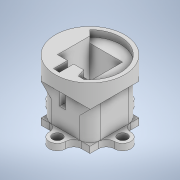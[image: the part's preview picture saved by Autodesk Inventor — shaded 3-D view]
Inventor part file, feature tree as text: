
AUTODESK INVENTOR PART (.ipt)
format: ipt  version: 2022 (Build 260153000, 153)  size: 370,688 bytes
history: native  units: in
note: dims shown in document units (in); Inventor stores cm internally (conversion verified against a paired STEP export)
features: projected_geometry x8, extrude x7, sketch x7, chamfer x2, fillet x2
ambient origin geometry x8: Origin, YZ Plane, XZ Plane, XY Plane, X Axis, Y Axis, Z Axis, Center Point
bodies: Solid1 (feature_tree)
feature tree (26):
  extrude  "Extrusion1"  Depth=0.3986in
  extrude  "Extrusion2"  Depth=0.1in
  extrude  "Extrusion3"  Depth=0.1in
  extrude  "Extrusion4"  Depth=0.315in
  extrude  "Extrusion5"  Depth=0.0787in TaperAngle=0.0deg
  chamfer  "Chamfer4"  Angle=90.0deg  [1 undecoded]
  chamfer  "Chamfer5"  Angle=90.0deg  [1 undecoded]
  extrude  "Extrusion6"  Depth=0.0787in TaperAngle=0.0deg
  fillet  "Fillet2"  [1 undecoded]
  extrude  "Extrusion7"  TaperAngle=90.0deg  [1 undecoded]
  fillet  "Fillet3"  Radius=0.75in
  sketch  "Sketch1"  dims[d0=0.3986in d1=0.3986in]
  sketch  "Sketch2"  dims[d2=0.1in d3=0.1in]
  projected_geometry  "Projected Loop1"
  sketch  "Sketch3"  dims[d4=0.1in d5=0.1in]
  sketch  "Sketch4"  dims[d6=0.315in d7=0.0in d8=0.05in]
  projected_geometry  "Projected Loop2"
  projected_geometry  "Projected Loop3"
  projected_geometry  "Projected Loop4"
  sketch  "Sketch5"  dims[d9=0.4331in d10=0.0in d11=0.0787in d12=0.0in]
  projected_geometry  "Projected Loop5"
  projected_geometry  "Projected Loop6"
  sketch  "Sketch6"  dims[d15=0.1in]
  projected_geometry  "Projected Loop7"
  sketch  "Sketch7"  dims[d16=0.1in d17=90.0deg d18=90.0deg d19=0.0787in d20=0.0in d31=90.0deg d32=90.0deg d33=0.75in d34=0.0787in d35=0.0in d36=0.1239in d37=0.125in d38=45.0deg d39=0.121in d40=0.125in d41=45.0deg d42=0.1in d43=0.2in d44=0.1in d45=0.2in d46=0.1in d47=0.1181in d48=0.1in d49=0.1181in d50=0.0787in d51=0.0in d52=0.1in d53=0.2in d54=0.1in d55=0.1in d56=0.2in d57=0.1in d58=0.1in d59=0.1181in d60=0.1181in d61=0.025in d62=0.0787in d63=0.0in d64=0.125in]
  projected_geometry  "Projected Loop8"
note: 4 required parameter values undecoded (feature->parameter linkage not recoverable at this tier; creation-order binding heuristic only, values carry confidence <= 0.55)
